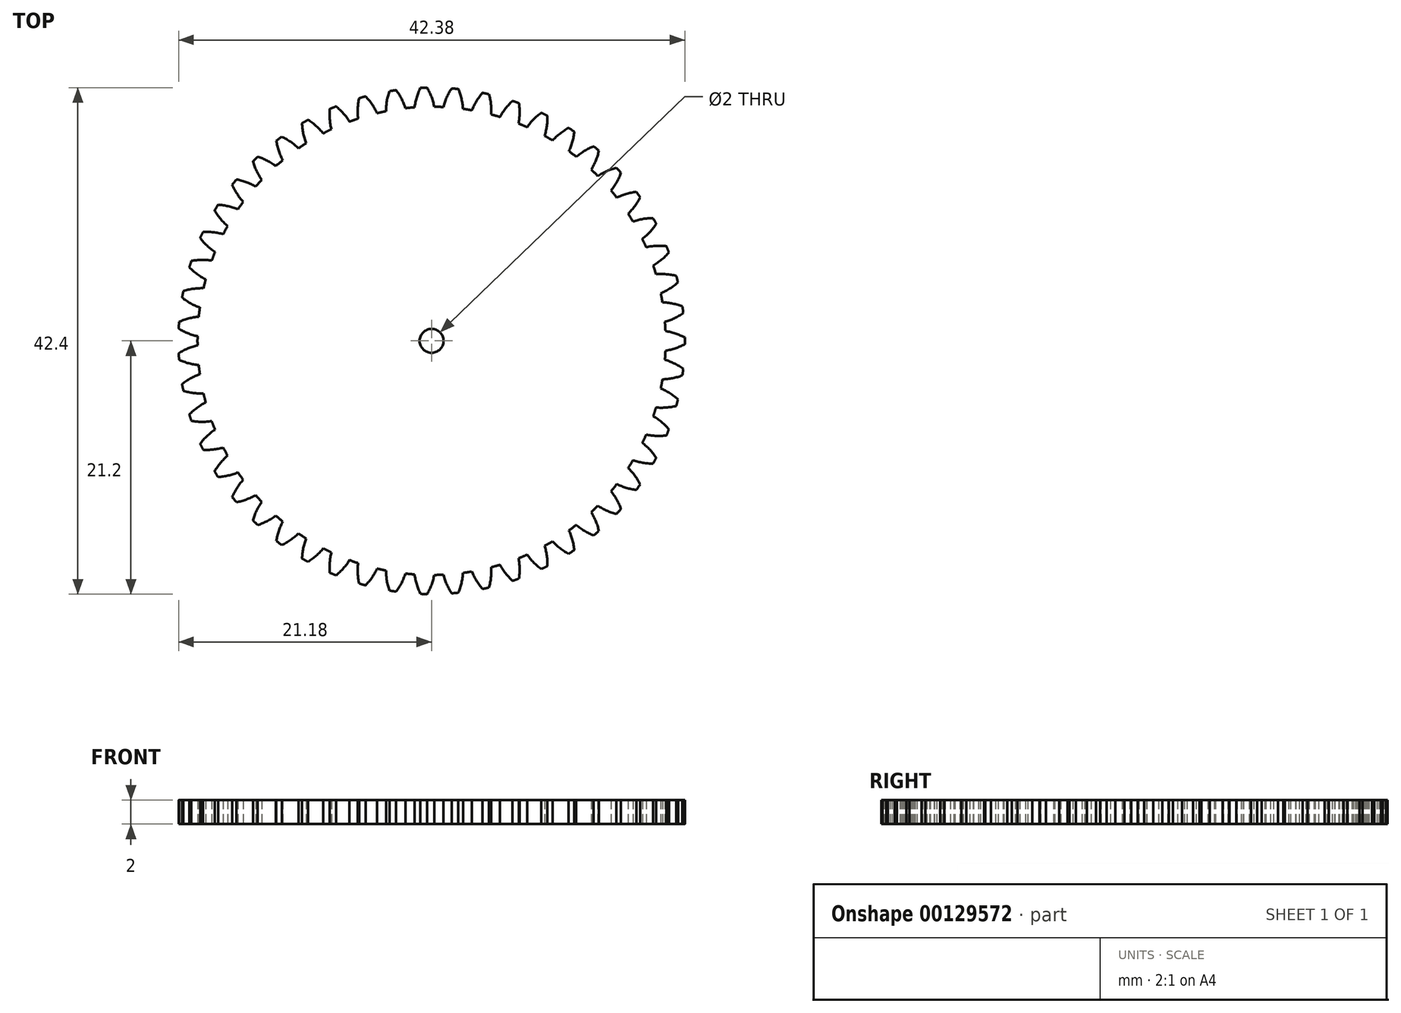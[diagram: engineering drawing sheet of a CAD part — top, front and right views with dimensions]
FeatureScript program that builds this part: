
annotation { "Feature Type Name" : "Feature", "Feature Type Description" : "" }
export const myFeature = defineFeature(function(context is Context, id is Id, definition is map)
    precondition{}
    {
        {
            var Q0;
            Q0=qCreatedBy(makeId("Top.planeOp"),FACE);
            var sketch = newSketch(context, id + "F0", { "sketchPlane" : qUnion([Q0])});
            skCircle(sketch, "E0", {"center": v(0, 0) * mm, "radius": 19.6 * mm, "construction": true});
            skCircle(sketch, "E1", {"center": v(0, 0) * mm, "radius": 20.4 * mm, "construction": true});
            skCircle(sketch, "E2", {"center": v(0, 0) * mm, "radius": 21.2 * mm, "construction": true});
            skLineSegment(sketch, "E3", {"start": v(0, 0) * mm, "end": v(0, 21.75) * mm, "construction": true});
            skLineSegment(sketch, "E4", {"start": v(0, 0) * mm, "end": v(-0.67, 21.71) * mm, "construction": true});
            skLineSegment(sketch, "E5", {"start": v(0, 20.4) * mm, "end": v(-10.54, 20.4) * mm, "construction": true});
            skLineSegment(sketch, "E6", {"start": v(0, 20.4) * mm, "end": v(-10.68, 16.51) * mm, "construction": true});
            skCircle(sketch, "E7", {"center": v(0, 20.4) * mm, "radius": 5.1 * mm, "construction": true});
            skCircle(sketch, "E8", {"center": v(-4.8, 18.66) * mm, "radius": 5.1 * mm, "construction": true});
            skArc(sketch, "E9", {"start": v(-9.58, 20.4) * mm, "mid": v(-9.8, 19.59) * mm, "end": v(-9.9, 18.75) * mm});
            skPoint(sketch, "E10.center", {"position": v(4.35, 4.65) * mm});
            skCircle(sketch, "E11", {"center": v(0, 0) * mm, "radius": 1 * mm});
            skArc(sketch, "E12", {"start": v(0.22, 19.6) * mm, "mid": v(0, 20.42) * mm, "end": v(-0.37, 21.2) * mm});
            skArc(sketch, "E13.MirrorCS", {"start": v(-1.43, 19.55) * mm, "mid": v(-1.25, 20.38) * mm, "end": v(-0.94, 21.18) * mm});
            skArc(sketch, "E14", {"start": v(-0.37, 21.2) * mm, "mid": v(-0.65, 21.19) * mm, "end": v(-0.94, 21.18) * mm});
            skArc(sketch, "E15.1.0", {"start": v(-2.97, 21) * mm, "mid": v(-3.25, 20.95) * mm, "end": v(-3.53, 20.9) * mm});
            skArc(sketch, "E15.1.1", {"start": v(-2.2, 19.48) * mm, "mid": v(-2.52, 20.27) * mm, "end": v(-2.97, 21) * mm});
            skArc(sketch, "E15.1.2", {"start": v(-3.82, 19.22) * mm, "mid": v(-3.74, 20.08) * mm, "end": v(-3.53, 20.9) * mm});
            skArc(sketch, "E15.2.0", {"start": v(-5.53, 20.47) * mm, "mid": v(-5.8, 20.4) * mm, "end": v(-6.07, 20.31) * mm});
            skArc(sketch, "E15.2.1", {"start": v(-4.57, 19.06) * mm, "mid": v(-4.99, 19.8) * mm, "end": v(-5.53, 20.47) * mm});
            skArc(sketch, "E15.2.2", {"start": v(-6.15, 18.6) * mm, "mid": v(-6.18, 19.46) * mm, "end": v(-6.07, 20.31) * mm});
            skArc(sketch, "E15.3.0", {"start": v(-8, 19.63) * mm, "mid": v(-8.26, 19.52) * mm, "end": v(-8.52, 19.41) * mm});
            skArc(sketch, "E15.3.1", {"start": v(-6.88, 18.35) * mm, "mid": v(-7.39, 19.04) * mm, "end": v(-8, 19.63) * mm});
            skArc(sketch, "E15.3.2", {"start": v(-8.4, 17.71) * mm, "mid": v(-8.53, 18.56) * mm, "end": v(-8.52, 19.41) * mm});
            skArc(sketch, "E15.4.0", {"start": v(-10.35, 18.5) * mm, "mid": v(-10.6, 18.36) * mm, "end": v(-10.84, 18.22) * mm});
            skArc(sketch, "E15.4.1", {"start": v(-9.08, 17.37) * mm, "mid": v(-9.67, 17.99) * mm, "end": v(-10.35, 18.5) * mm});
            skArc(sketch, "E15.4.2", {"start": v(-10.5, 16.55) * mm, "mid": v(-10.74, 17.37) * mm, "end": v(-10.84, 18.22) * mm});
            skArc(sketch, "E15.5.0", {"start": v(-12.55, 17.09) * mm, "mid": v(-12.78, 16.92) * mm, "end": v(-13, 16.75) * mm});
            skArc(sketch, "E15.5.1", {"start": v(-11.14, 16.12) * mm, "mid": v(-11.8, 16.66) * mm, "end": v(-12.55, 17.09) * mm});
            skArc(sketch, "E15.5.2", {"start": v(-12.46, 15.13) * mm, "mid": v(-12.8, 15.92) * mm, "end": v(-13, 16.75) * mm});
            skArc(sketch, "E15.6.0", {"start": v(-14.55, 15.41) * mm, "mid": v(-14.76, 15.22) * mm, "end": v(-14.96, 15.02) * mm});
            skArc(sketch, "E15.6.1", {"start": v(-13.04, 14.63) * mm, "mid": v(-13.76, 15.09) * mm, "end": v(-14.55, 15.41) * mm});
            skArc(sketch, "E15.6.2", {"start": v(-14.22, 13.49) * mm, "mid": v(-14.66, 14.22) * mm, "end": v(-14.96, 15.02) * mm});
            skArc(sketch, "E15.7.0", {"start": v(-16.34, 13.5) * mm, "mid": v(-16.52, 13.3) * mm, "end": v(-16.7, 13.07) * mm});
            skArc(sketch, "E15.7.1", {"start": v(-14.74, 12.92) * mm, "mid": v(-15.51, 13.28) * mm, "end": v(-16.34, 13.5) * mm});
            skArc(sketch, "E15.7.2", {"start": v(-15.77, 11.64) * mm, "mid": v(-16.3, 12.31) * mm, "end": v(-16.7, 13.07) * mm});
            skArc(sketch, "E15.8.0", {"start": v(-17.87, 11.4) * mm, "mid": v(-18.02, 11.16) * mm, "end": v(-18.17, 10.92) * mm});
            skArc(sketch, "E15.8.1", {"start": v(-16.22, 11) * mm, "mid": v(-17.03, 11.27) * mm, "end": v(-17.87, 11.4) * mm});
            skArc(sketch, "E15.8.2", {"start": v(-17.08, 9.6) * mm, "mid": v(-17.68, 10.22) * mm, "end": v(-18.17, 10.92) * mm});
            skArc(sketch, "E15.9.0", {"start": v(-19.14, 9.12) * mm, "mid": v(-19.26, 8.86) * mm, "end": v(-19.38, 8.6) * mm});
            skArc(sketch, "E15.9.1", {"start": v(-17.45, 8.93) * mm, "mid": v(-18.29, 9.1) * mm, "end": v(-19.14, 9.12) * mm});
            skArc(sketch, "E15.9.2", {"start": v(-18.13, 7.44) * mm, "mid": v(-18.8, 7.97) * mm, "end": v(-19.38, 8.6) * mm});
            skArc(sketch, "E15.10.0", {"start": v(-20.11, 6.7) * mm, "mid": v(-20.2, 6.43) * mm, "end": v(-20.29, 6.16) * mm});
            skArc(sketch, "E15.10.1", {"start": v(-18.41, 6.72) * mm, "mid": v(-19.26, 6.78) * mm, "end": v(-20.11, 6.7) * mm});
            skArc(sketch, "E15.10.2", {"start": v(-18.91, 5.15) * mm, "mid": v(-19.64, 5.6) * mm, "end": v(-20.29, 6.16) * mm});
            skArc(sketch, "E15.11.0", {"start": v(-20.79, 4.17) * mm, "mid": v(-20.84, 3.9) * mm, "end": v(-20.89, 3.62) * mm});
            skArc(sketch, "E15.11.1", {"start": v(-19.1, 4.4) * mm, "mid": v(-19.95, 4.36) * mm, "end": v(-20.79, 4.17) * mm});
            skArc(sketch, "E15.11.2", {"start": v(-19.4, 2.79) * mm, "mid": v(-20.18, 3.14) * mm, "end": v(-20.89, 3.62) * mm});
            skArc(sketch, "E15.12.0", {"start": v(-21.14, 1.59) * mm, "mid": v(-21.16, 1.3) * mm, "end": v(-21.18, 1.02) * mm});
            skArc(sketch, "E15.12.1", {"start": v(-19.5, 2.03) * mm, "mid": v(-20.34, 1.88) * mm, "end": v(-21.14, 1.59) * mm});
            skArc(sketch, "E15.12.2", {"start": v(-19.6, 0.38) * mm, "mid": v(-20.41, 0.64) * mm, "end": v(-21.18, 1.02) * mm});
            skArc(sketch, "E15.13.0", {"start": v(-21.18, -1.02) * mm, "mid": v(-21.16, -1.3) * mm, "end": v(-21.14, -1.59) * mm});
            skArc(sketch, "E15.13.1", {"start": v(-19.6, -0.38) * mm, "mid": v(-20.41, -0.64) * mm, "end": v(-21.18, -1.02) * mm});
            skArc(sketch, "E15.13.2", {"start": v(-19.5, -2.03) * mm, "mid": v(-20.34, -1.88) * mm, "end": v(-21.14, -1.59) * mm});
            skArc(sketch, "E15.14.0", {"start": v(-20.89, -3.62) * mm, "mid": v(-20.84, -3.9) * mm, "end": v(-20.79, -4.17) * mm});
            skArc(sketch, "E15.14.1", {"start": v(-19.4, -2.79) * mm, "mid": v(-20.18, -3.14) * mm, "end": v(-20.89, -3.62) * mm});
            skArc(sketch, "E15.14.2", {"start": v(-19.1, -4.4) * mm, "mid": v(-19.95, -4.36) * mm, "end": v(-20.79, -4.17) * mm});
            skArc(sketch, "E15.15.0", {"start": v(-20.29, -6.16) * mm, "mid": v(-20.2, -6.43) * mm, "end": v(-20.11, -6.7) * mm});
            skArc(sketch, "E15.15.1", {"start": v(-18.91, -5.15) * mm, "mid": v(-19.64, -5.6) * mm, "end": v(-20.29, -6.16) * mm});
            skArc(sketch, "E15.15.2", {"start": v(-18.41, -6.72) * mm, "mid": v(-19.26, -6.78) * mm, "end": v(-20.11, -6.7) * mm});
            skArc(sketch, "E15.16.0", {"start": v(-19.38, -8.6) * mm, "mid": v(-19.26, -8.86) * mm, "end": v(-19.14, -9.12) * mm});
            skArc(sketch, "E15.16.1", {"start": v(-18.13, -7.44) * mm, "mid": v(-18.8, -7.97) * mm, "end": v(-19.38, -8.6) * mm});
            skArc(sketch, "E15.16.2", {"start": v(-17.45, -8.93) * mm, "mid": v(-18.29, -9.1) * mm, "end": v(-19.14, -9.12) * mm});
            skArc(sketch, "E15.17.0", {"start": v(-18.17, -10.92) * mm, "mid": v(-18.02, -11.16) * mm, "end": v(-17.87, -11.4) * mm});
            skArc(sketch, "E15.17.1", {"start": v(-17.08, -9.6) * mm, "mid": v(-17.68, -10.22) * mm, "end": v(-18.17, -10.92) * mm});
            skArc(sketch, "E15.17.2", {"start": v(-16.22, -11) * mm, "mid": v(-17.03, -11.27) * mm, "end": v(-17.87, -11.4) * mm});
            skArc(sketch, "E15.18.0", {"start": v(-16.7, -13.07) * mm, "mid": v(-16.52, -13.3) * mm, "end": v(-16.34, -13.5) * mm});
            skArc(sketch, "E15.18.1", {"start": v(-15.77, -11.64) * mm, "mid": v(-16.3, -12.31) * mm, "end": v(-16.7, -13.07) * mm});
            skArc(sketch, "E15.18.2", {"start": v(-14.74, -12.92) * mm, "mid": v(-15.51, -13.28) * mm, "end": v(-16.34, -13.5) * mm});
            skArc(sketch, "E15.19.0", {"start": v(-14.96, -15.02) * mm, "mid": v(-14.76, -15.22) * mm, "end": v(-14.55, -15.41) * mm});
            skArc(sketch, "E15.19.1", {"start": v(-14.22, -13.49) * mm, "mid": v(-14.66, -14.22) * mm, "end": v(-14.96, -15.02) * mm});
            skArc(sketch, "E15.19.2", {"start": v(-13.04, -14.63) * mm, "mid": v(-13.76, -15.09) * mm, "end": v(-14.55, -15.41) * mm});
            skArc(sketch, "E15.20.0", {"start": v(-13, -16.75) * mm, "mid": v(-12.78, -16.92) * mm, "end": v(-12.55, -17.09) * mm});
            skArc(sketch, "E15.20.1", {"start": v(-12.46, -15.13) * mm, "mid": v(-12.8, -15.92) * mm, "end": v(-13, -16.75) * mm});
            skArc(sketch, "E15.20.2", {"start": v(-11.14, -16.12) * mm, "mid": v(-11.8, -16.66) * mm, "end": v(-12.55, -17.09) * mm});
            skArc(sketch, "E15.21.0", {"start": v(-10.84, -18.22) * mm, "mid": v(-10.6, -18.36) * mm, "end": v(-10.35, -18.5) * mm});
            skArc(sketch, "E15.21.1", {"start": v(-10.5, -16.55) * mm, "mid": v(-10.74, -17.37) * mm, "end": v(-10.84, -18.22) * mm});
            skArc(sketch, "E15.21.2", {"start": v(-9.08, -17.37) * mm, "mid": v(-9.67, -17.99) * mm, "end": v(-10.35, -18.5) * mm});
            skArc(sketch, "E15.22.0", {"start": v(-8.52, -19.41) * mm, "mid": v(-8.26, -19.52) * mm, "end": v(-8, -19.63) * mm});
            skArc(sketch, "E15.22.1", {"start": v(-8.4, -17.71) * mm, "mid": v(-8.53, -18.56) * mm, "end": v(-8.52, -19.41) * mm});
            skArc(sketch, "E15.22.2", {"start": v(-6.88, -18.35) * mm, "mid": v(-7.39, -19.04) * mm, "end": v(-8, -19.63) * mm});
            skArc(sketch, "E15.23.0", {"start": v(-6.07, -20.31) * mm, "mid": v(-5.8, -20.4) * mm, "end": v(-5.53, -20.47) * mm});
            skArc(sketch, "E15.23.1", {"start": v(-6.15, -18.6) * mm, "mid": v(-6.18, -19.46) * mm, "end": v(-6.07, -20.31) * mm});
            skArc(sketch, "E15.23.2", {"start": v(-4.57, -19.06) * mm, "mid": v(-4.99, -19.8) * mm, "end": v(-5.53, -20.47) * mm});
            skArc(sketch, "E15.24.0", {"start": v(-3.53, -20.9) * mm, "mid": v(-3.25, -20.95) * mm, "end": v(-2.97, -21) * mm});
            skArc(sketch, "E15.24.1", {"start": v(-3.82, -19.22) * mm, "mid": v(-3.74, -20.08) * mm, "end": v(-3.53, -20.9) * mm});
            skArc(sketch, "E15.24.2", {"start": v(-2.2, -19.48) * mm, "mid": v(-2.52, -20.27) * mm, "end": v(-2.97, -21) * mm});
            skArc(sketch, "E15.25.0", {"start": v(-0.94, -21.18) * mm, "mid": v(-0.65, -21.19) * mm, "end": v(-0.37, -21.2) * mm});
            skArc(sketch, "E15.25.1", {"start": v(-1.43, -19.55) * mm, "mid": v(-1.25, -20.38) * mm, "end": v(-0.94, -21.18) * mm});
            skArc(sketch, "E15.25.2", {"start": v(0.22, -19.6) * mm, "mid": v(0, -20.42) * mm, "end": v(-0.37, -21.2) * mm});
            skArc(sketch, "E15.26.0", {"start": v(1.67, -21.13) * mm, "mid": v(1.96, -21.1) * mm, "end": v(2.24, -21.08) * mm});
            skArc(sketch, "E15.26.1", {"start": v(0.99, -19.58) * mm, "mid": v(1.27, -20.38) * mm, "end": v(1.67, -21.13) * mm});
            skArc(sketch, "E15.26.2", {"start": v(2.63, -19.42) * mm, "mid": v(2.5, -20.27) * mm, "end": v(2.24, -21.08) * mm});
            skArc(sketch, "E15.27.0", {"start": v(4.26, -20.77) * mm, "mid": v(4.54, -20.7) * mm, "end": v(4.81, -20.65) * mm});
            skArc(sketch, "E15.27.1", {"start": v(3.39, -19.3) * mm, "mid": v(3.76, -20.07) * mm, "end": v(4.26, -20.77) * mm});
            skArc(sketch, "E15.27.2", {"start": v(5, -18.95) * mm, "mid": v(4.97, -19.8) * mm, "end": v(4.81, -20.65) * mm});
            skArc(sketch, "E15.28.0", {"start": v(6.78, -20.09) * mm, "mid": v(7.05, -20) * mm, "end": v(7.31, -19.9) * mm});
            skArc(sketch, "E15.28.1", {"start": v(5.73, -18.74) * mm, "mid": v(6.2, -19.46) * mm, "end": v(6.78, -20.09) * mm});
            skArc(sketch, "E15.28.2", {"start": v(7.28, -18.2) * mm, "mid": v(7.37, -19.05) * mm, "end": v(7.31, -19.9) * mm});
            skArc(sketch, "E15.29.0", {"start": v(9.2, -19.1) * mm, "mid": v(9.45, -18.98) * mm, "end": v(9.7, -18.85) * mm});
            skArc(sketch, "E15.29.1", {"start": v(8, -17.9) * mm, "mid": v(8.54, -18.55) * mm, "end": v(9.2, -19.1) * mm});
            skArc(sketch, "E15.29.2", {"start": v(9.47, -17.16) * mm, "mid": v(9.65, -18) * mm, "end": v(9.7, -18.85) * mm});
            skArc(sketch, "E15.30.0", {"start": v(11.47, -17.83) * mm, "mid": v(11.71, -17.67) * mm, "end": v(11.94, -17.51) * mm});
            skArc(sketch, "E15.30.1", {"start": v(10.13, -16.78) * mm, "mid": v(10.76, -17.36) * mm, "end": v(11.47, -17.83) * mm});
            skArc(sketch, "E15.30.2", {"start": v(11.5, -15.87) * mm, "mid": v(11.8, -16.67) * mm, "end": v(11.94, -17.51) * mm});
            skArc(sketch, "E15.31.0", {"start": v(13.58, -16.28) * mm, "mid": v(13.8, -16.1) * mm, "end": v(14, -15.91) * mm});
            skArc(sketch, "E15.31.1", {"start": v(12.12, -15.4) * mm, "mid": v(12.8, -15.9) * mm, "end": v(13.58, -16.28) * mm});
            skArc(sketch, "E15.31.2", {"start": v(13.37, -14.34) * mm, "mid": v(13.75, -15.1) * mm, "end": v(14, -15.91) * mm});
            skArc(sketch, "E15.32.0", {"start": v(15.48, -14.49) * mm, "mid": v(15.67, -14.28) * mm, "end": v(15.86, -14.07) * mm});
            skArc(sketch, "E15.32.1", {"start": v(13.92, -13.8) * mm, "mid": v(14.67, -14.21) * mm, "end": v(15.48, -14.49) * mm});
            skArc(sketch, "E15.32.2", {"start": v(15.03, -12.58) * mm, "mid": v(15.5, -13.3) * mm, "end": v(15.86, -14.07) * mm});
            skArc(sketch, "E15.33.0", {"start": v(17.14, -12.48) * mm, "mid": v(17.3, -12.25) * mm, "end": v(17.46, -12.02) * mm});
            skArc(sketch, "E15.33.1", {"start": v(15.5, -11.99) * mm, "mid": v(16.3, -12.3) * mm, "end": v(17.14, -12.48) * mm});
            skArc(sketch, "E15.33.2", {"start": v(16.46, -10.64) * mm, "mid": v(17.02, -11.29) * mm, "end": v(17.46, -12.02) * mm});
            skArc(sketch, "E15.34.0", {"start": v(18.54, -10.28) * mm, "mid": v(18.68, -10.03) * mm, "end": v(18.8, -9.78) * mm});
            skArc(sketch, "E15.34.1", {"start": v(16.86, -9.99) * mm, "mid": v(17.7, -10.2) * mm, "end": v(18.54, -10.28) * mm});
            skArc(sketch, "E15.34.2", {"start": v(17.64, -8.54) * mm, "mid": v(18.28, -9.11) * mm, "end": v(18.8, -9.78) * mm});
            skArc(sketch, "E15.35.0", {"start": v(19.66, -7.92) * mm, "mid": v(19.77, -7.66) * mm, "end": v(19.87, -7.4) * mm});
            skArc(sketch, "E15.35.1", {"start": v(17.96, -7.84) * mm, "mid": v(18.81, -7.95) * mm, "end": v(19.66, -7.92) * mm});
            skArc(sketch, "E15.35.2", {"start": v(18.56, -6.3) * mm, "mid": v(19.26, -6.8) * mm, "end": v(19.87, -7.4) * mm});
            skArc(sketch, "E15.36.0", {"start": v(20.49, -5.44) * mm, "mid": v(20.56, -5.17) * mm, "end": v(20.63, -4.9) * mm});
            skArc(sketch, "E15.36.1", {"start": v(18.8, -5.57) * mm, "mid": v(19.65, -5.58) * mm, "end": v(20.49, -5.44) * mm});
            skArc(sketch, "E15.36.2", {"start": v(19.2, -3.98) * mm, "mid": v(19.95, -4.38) * mm, "end": v(20.63, -4.9) * mm});
            skArc(sketch, "E15.37.0", {"start": v(21, -2.89) * mm, "mid": v(21.04, -2.6) * mm, "end": v(21.07, -2.32) * mm});
            skArc(sketch, "E15.37.1", {"start": v(19.33, -3.22) * mm, "mid": v(20.18, -3.12) * mm, "end": v(21, -2.89) * mm});
            skArc(sketch, "E15.37.2", {"start": v(19.54, -1.59) * mm, "mid": v(20.33, -1.9) * mm, "end": v(21.07, -2.32) * mm});
            skArc(sketch, "E15.38.0", {"start": v(21.2, -0.28) * mm, "mid": v(21.2, 0) * mm, "end": v(21.2, 0.28) * mm});
            skArc(sketch, "E15.38.1", {"start": v(19.58, -0.82) * mm, "mid": v(20.41, -0.62) * mm, "end": v(21.2, -0.28) * mm});
            skArc(sketch, "E15.38.2", {"start": v(19.58, 0.82) * mm, "mid": v(20.41, 0.62) * mm, "end": v(21.2, 0.28) * mm});
            skArc(sketch, "E15.39.0", {"start": v(21.07, 2.32) * mm, "mid": v(21.04, 2.6) * mm, "end": v(21, 2.89) * mm});
            skArc(sketch, "E15.39.1", {"start": v(19.54, 1.59) * mm, "mid": v(20.33, 1.9) * mm, "end": v(21.07, 2.32) * mm});
            skArc(sketch, "E15.39.2", {"start": v(19.33, 3.22) * mm, "mid": v(20.18, 3.12) * mm, "end": v(21, 2.89) * mm});
            skArc(sketch, "E15.40.0", {"start": v(20.63, 4.9) * mm, "mid": v(20.56, 5.17) * mm, "end": v(20.49, 5.44) * mm});
            skArc(sketch, "E15.40.1", {"start": v(19.2, 3.98) * mm, "mid": v(19.95, 4.38) * mm, "end": v(20.63, 4.9) * mm});
            skArc(sketch, "E15.40.2", {"start": v(18.8, 5.57) * mm, "mid": v(19.65, 5.58) * mm, "end": v(20.49, 5.44) * mm});
            skArc(sketch, "E15.41.0", {"start": v(19.87, 7.4) * mm, "mid": v(19.77, 7.66) * mm, "end": v(19.66, 7.92) * mm});
            skArc(sketch, "E15.41.1", {"start": v(18.56, 6.3) * mm, "mid": v(19.26, 6.8) * mm, "end": v(19.87, 7.4) * mm});
            skArc(sketch, "E15.41.2", {"start": v(17.96, 7.84) * mm, "mid": v(18.81, 7.95) * mm, "end": v(19.66, 7.92) * mm});
            skArc(sketch, "E15.42.0", {"start": v(18.8, 9.78) * mm, "mid": v(18.68, 10.03) * mm, "end": v(18.54, 10.28) * mm});
            skArc(sketch, "E15.42.1", {"start": v(17.64, 8.54) * mm, "mid": v(18.28, 9.11) * mm, "end": v(18.8, 9.78) * mm});
            skArc(sketch, "E15.42.2", {"start": v(16.86, 9.99) * mm, "mid": v(17.7, 10.2) * mm, "end": v(18.54, 10.28) * mm});
            skArc(sketch, "E15.43.0", {"start": v(17.46, 12.02) * mm, "mid": v(17.3, 12.25) * mm, "end": v(17.14, 12.48) * mm});
            skArc(sketch, "E15.43.1", {"start": v(16.46, 10.64) * mm, "mid": v(17.02, 11.29) * mm, "end": v(17.46, 12.02) * mm});
            skArc(sketch, "E15.43.2", {"start": v(15.5, 11.99) * mm, "mid": v(16.3, 12.3) * mm, "end": v(17.14, 12.48) * mm});
            skArc(sketch, "E15.44.0", {"start": v(15.86, 14.07) * mm, "mid": v(15.67, 14.28) * mm, "end": v(15.48, 14.49) * mm});
            skArc(sketch, "E15.44.1", {"start": v(15.03, 12.58) * mm, "mid": v(15.5, 13.3) * mm, "end": v(15.86, 14.07) * mm});
            skArc(sketch, "E15.44.2", {"start": v(13.92, 13.8) * mm, "mid": v(14.67, 14.21) * mm, "end": v(15.48, 14.49) * mm});
            skArc(sketch, "E15.45.0", {"start": v(14, 15.91) * mm, "mid": v(13.8, 16.1) * mm, "end": v(13.58, 16.28) * mm});
            skArc(sketch, "E15.45.1", {"start": v(13.37, 14.34) * mm, "mid": v(13.75, 15.1) * mm, "end": v(14, 15.91) * mm});
            skArc(sketch, "E15.45.2", {"start": v(12.12, 15.4) * mm, "mid": v(12.8, 15.9) * mm, "end": v(13.58, 16.28) * mm});
            skArc(sketch, "E15.46.0", {"start": v(11.94, 17.51) * mm, "mid": v(11.71, 17.67) * mm, "end": v(11.47, 17.83) * mm});
            skArc(sketch, "E15.46.1", {"start": v(11.5, 15.87) * mm, "mid": v(11.8, 16.67) * mm, "end": v(11.94, 17.51) * mm});
            skArc(sketch, "E15.46.2", {"start": v(10.13, 16.78) * mm, "mid": v(10.76, 17.36) * mm, "end": v(11.47, 17.83) * mm});
            skArc(sketch, "E15.47.0", {"start": v(9.7, 18.85) * mm, "mid": v(9.45, 18.98) * mm, "end": v(9.2, 19.1) * mm});
            skArc(sketch, "E15.47.1", {"start": v(9.47, 17.16) * mm, "mid": v(9.65, 18) * mm, "end": v(9.7, 18.85) * mm});
            skArc(sketch, "E15.47.2", {"start": v(8, 17.9) * mm, "mid": v(8.54, 18.55) * mm, "end": v(9.2, 19.1) * mm});
            skArc(sketch, "E16.4.48.0", {"start": v(7.28, 18.2) * mm, "mid": v(7.37, 19.05) * mm, "end": v(7.31, 19.9) * mm});
            skArc(sketch, "E16.8.48.0", {"start": v(5.73, 18.74) * mm, "mid": v(6.2, 19.46) * mm, "end": v(6.78, 20.09) * mm});
            skArc(sketch, "E16.10.48.0", {"start": v(7.31, 19.9) * mm, "mid": v(7.05, 20) * mm, "end": v(6.78, 20.09) * mm});
            skArc(sketch, "E16.4.49.0", {"start": v(5, 18.95) * mm, "mid": v(4.97, 19.8) * mm, "end": v(4.81, 20.65) * mm});
            skArc(sketch, "E16.8.49.0", {"start": v(3.39, 19.3) * mm, "mid": v(3.76, 20.07) * mm, "end": v(4.26, 20.77) * mm});
            skArc(sketch, "E16.10.49.0", {"start": v(4.81, 20.65) * mm, "mid": v(4.54, 20.7) * mm, "end": v(4.26, 20.77) * mm});
            skArc(sketch, "E17", {"start": v(0.99, 19.58) * mm, "mid": v(0.6, 19.6) * mm, "end": v(0.22, 19.6) * mm});
            skArc(sketch, "E18.1.0", {"start": v(-1.43, 19.55) * mm, "mid": v(-1.8, 19.52) * mm, "end": v(-2.2, 19.48) * mm});
            skArc(sketch, "E18.2.0", {"start": v(-3.82, 19.22) * mm, "mid": v(-4.2, 19.15) * mm, "end": v(-4.57, 19.06) * mm});
            skArc(sketch, "E18.3.0", {"start": v(-6.15, 18.6) * mm, "mid": v(-6.51, 18.49) * mm, "end": v(-6.88, 18.35) * mm});
            skArc(sketch, "E18.4.0", {"start": v(-8.4, 17.71) * mm, "mid": v(-8.74, 17.55) * mm, "end": v(-9.08, 17.37) * mm});
            skArc(sketch, "E18.5.0", {"start": v(-10.5, 16.55) * mm, "mid": v(-10.83, 16.34) * mm, "end": v(-11.14, 16.12) * mm});
            skArc(sketch, "E18.6.0", {"start": v(-12.46, 15.13) * mm, "mid": v(-12.75, 14.88) * mm, "end": v(-13.04, 14.63) * mm});
            skArc(sketch, "E18.7.0", {"start": v(-14.22, 13.49) * mm, "mid": v(-14.48, 13.2) * mm, "end": v(-14.74, 12.92) * mm});
            skArc(sketch, "E18.8.0", {"start": v(-15.77, 11.64) * mm, "mid": v(-16, 11.32) * mm, "end": v(-16.22, 11) * mm});
            skArc(sketch, "E18.9.0", {"start": v(-17.08, 9.6) * mm, "mid": v(-17.27, 9.27) * mm, "end": v(-17.45, 8.93) * mm});
            skArc(sketch, "E18.10.0", {"start": v(-18.13, 7.44) * mm, "mid": v(-18.28, 7.08) * mm, "end": v(-18.41, 6.72) * mm});
            skArc(sketch, "E18.11.0", {"start": v(-18.91, 5.15) * mm, "mid": v(-19, 4.78) * mm, "end": v(-19.1, 4.4) * mm});
            skArc(sketch, "E18.12.0", {"start": v(-19.4, 2.79) * mm, "mid": v(-19.45, 2.4) * mm, "end": v(-19.5, 2.03) * mm});
            skArc(sketch, "E18.13.0", {"start": v(-19.6, 0.38) * mm, "mid": v(-19.6, 0) * mm, "end": v(-19.6, -0.38) * mm});
            skArc(sketch, "E18.14.0", {"start": v(-19.5, -2.03) * mm, "mid": v(-19.45, -2.4) * mm, "end": v(-19.4, -2.79) * mm});
            skArc(sketch, "E18.15.0", {"start": v(-19.1, -4.4) * mm, "mid": v(-19, -4.78) * mm, "end": v(-18.91, -5.15) * mm});
            skArc(sketch, "E18.16.0", {"start": v(-18.41, -6.72) * mm, "mid": v(-18.28, -7.08) * mm, "end": v(-18.13, -7.44) * mm});
            skArc(sketch, "E18.17.0", {"start": v(-17.45, -8.93) * mm, "mid": v(-17.27, -9.27) * mm, "end": v(-17.08, -9.6) * mm});
            skArc(sketch, "E18.18.0", {"start": v(-16.22, -11) * mm, "mid": v(-16, -11.32) * mm, "end": v(-15.77, -11.64) * mm});
            skArc(sketch, "E18.19.0", {"start": v(-14.74, -12.92) * mm, "mid": v(-14.48, -13.2) * mm, "end": v(-14.22, -13.49) * mm});
            skArc(sketch, "E18.20.0", {"start": v(-13.04, -14.63) * mm, "mid": v(-12.75, -14.88) * mm, "end": v(-12.46, -15.13) * mm});
            skArc(sketch, "E18.21.0", {"start": v(-11.14, -16.12) * mm, "mid": v(-10.83, -16.34) * mm, "end": v(-10.5, -16.55) * mm});
            skArc(sketch, "E18.22.0", {"start": v(-9.08, -17.37) * mm, "mid": v(-8.74, -17.55) * mm, "end": v(-8.4, -17.71) * mm});
            skArc(sketch, "E18.23.0", {"start": v(-6.88, -18.35) * mm, "mid": v(-6.51, -18.49) * mm, "end": v(-6.15, -18.6) * mm});
            skArc(sketch, "E18.24.0", {"start": v(-4.57, -19.06) * mm, "mid": v(-4.2, -19.15) * mm, "end": v(-3.82, -19.22) * mm});
            skArc(sketch, "E18.25.0", {"start": v(-2.2, -19.48) * mm, "mid": v(-1.8, -19.52) * mm, "end": v(-1.43, -19.55) * mm});
            skArc(sketch, "E18.26.0", {"start": v(0.22, -19.6) * mm, "mid": v(0.6, -19.6) * mm, "end": v(0.99, -19.58) * mm});
            skArc(sketch, "E18.27.0", {"start": v(2.63, -19.42) * mm, "mid": v(3, -19.37) * mm, "end": v(3.39, -19.3) * mm});
            skArc(sketch, "E18.28.0", {"start": v(5, -18.95) * mm, "mid": v(5.36, -18.85) * mm, "end": v(5.73, -18.74) * mm});
            skArc(sketch, "E18.29.0", {"start": v(7.28, -18.2) * mm, "mid": v(7.64, -18.05) * mm, "end": v(8, -17.9) * mm});
            skArc(sketch, "E18.30.0", {"start": v(9.47, -17.16) * mm, "mid": v(9.8, -16.97) * mm, "end": v(10.13, -16.78) * mm});
            skArc(sketch, "E18.31.0", {"start": v(11.5, -15.87) * mm, "mid": v(11.81, -15.64) * mm, "end": v(12.12, -15.4) * mm});
            skArc(sketch, "E18.32.0", {"start": v(13.37, -14.34) * mm, "mid": v(13.64, -14.07) * mm, "end": v(13.92, -13.8) * mm});
            skArc(sketch, "E18.33.0", {"start": v(15.03, -12.58) * mm, "mid": v(15.27, -12.29) * mm, "end": v(15.5, -11.99) * mm});
            skArc(sketch, "E18.34.0", {"start": v(16.46, -10.64) * mm, "mid": v(16.66, -10.32) * mm, "end": v(16.86, -9.99) * mm});
            skArc(sketch, "E18.35.0", {"start": v(17.64, -8.54) * mm, "mid": v(17.8, -8.2) * mm, "end": v(17.96, -7.84) * mm});
            skArc(sketch, "E18.36.0", {"start": v(18.56, -6.3) * mm, "mid": v(18.68, -5.94) * mm, "end": v(18.8, -5.57) * mm});
            skArc(sketch, "E18.37.0", {"start": v(19.2, -3.98) * mm, "mid": v(19.27, -3.6) * mm, "end": v(19.33, -3.22) * mm});
            skArc(sketch, "E18.38.0", {"start": v(19.54, -1.59) * mm, "mid": v(19.56, -1.2) * mm, "end": v(19.58, -0.82) * mm});
            skArc(sketch, "E18.39.0", {"start": v(19.58, 0.82) * mm, "mid": v(19.56, 1.2) * mm, "end": v(19.54, 1.59) * mm});
            skArc(sketch, "E18.40.0", {"start": v(19.33, 3.22) * mm, "mid": v(19.27, 3.6) * mm, "end": v(19.2, 3.98) * mm});
            skArc(sketch, "E18.41.0", {"start": v(18.8, 5.57) * mm, "mid": v(18.68, 5.94) * mm, "end": v(18.56, 6.3) * mm});
            skArc(sketch, "E18.42.0", {"start": v(17.96, 7.84) * mm, "mid": v(17.8, 8.2) * mm, "end": v(17.64, 8.54) * mm});
            skArc(sketch, "E18.43.0", {"start": v(16.86, 9.99) * mm, "mid": v(16.66, 10.32) * mm, "end": v(16.46, 10.64) * mm});
            skArc(sketch, "E18.44.0", {"start": v(15.5, 11.99) * mm, "mid": v(15.27, 12.29) * mm, "end": v(15.03, 12.58) * mm});
            skArc(sketch, "E18.45.0", {"start": v(13.92, 13.8) * mm, "mid": v(13.64, 14.07) * mm, "end": v(13.37, 14.34) * mm});
            skArc(sketch, "E18.46.0", {"start": v(12.12, 15.4) * mm, "mid": v(11.81, 15.64) * mm, "end": v(11.5, 15.87) * mm});
            skArc(sketch, "E18.47.0", {"start": v(10.13, 16.78) * mm, "mid": v(9.8, 16.97) * mm, "end": v(9.47, 17.16) * mm});
            skArc(sketch, "E18.48.0", {"start": v(8, 17.9) * mm, "mid": v(7.64, 18.05) * mm, "end": v(7.28, 18.2) * mm});
            skArc(sketch, "E18.49.0", {"start": v(5.73, 18.74) * mm, "mid": v(5.36, 18.85) * mm, "end": v(5, 18.95) * mm});
            skArc(sketch, "E19.4.50.0", {"start": v(2.63, 19.42) * mm, "mid": v(2.5, 20.27) * mm, "end": v(2.24, 21.08) * mm});
            skArc(sketch, "E19.8.50.0", {"start": v(0.99, 19.58) * mm, "mid": v(1.27, 20.38) * mm, "end": v(1.67, 21.13) * mm});
            skArc(sketch, "E19.10.50.0", {"start": v(2.24, 21.08) * mm, "mid": v(1.96, 21.1) * mm, "end": v(1.67, 21.13) * mm});
            skArc(sketch, "E20.3.50.0", {"start": v(3.39, 19.3) * mm, "mid": v(3, 19.37) * mm, "end": v(2.63, 19.42) * mm});
            skSolve(sketch);
        }
        {
            var Q0;
            Q0 = qSketchRegion(id + "F0", true);
            var Q1;
            Q1=makeQuery(id+"F0.imprint","IMPRINT",FACE,{"disambiguationData":[TD([[makeQuery(id+"F0.imprint","IMPRINT",EDGE,{"derivedFrom":sQuery(id+"F0.wireOp",EDGE,"E11")}),-1.0]])]});
            extrude(context, id + "F1", {"entities" : qUnion([Q0, Q1]), "depth" : 2 * mm});
        }
    });
